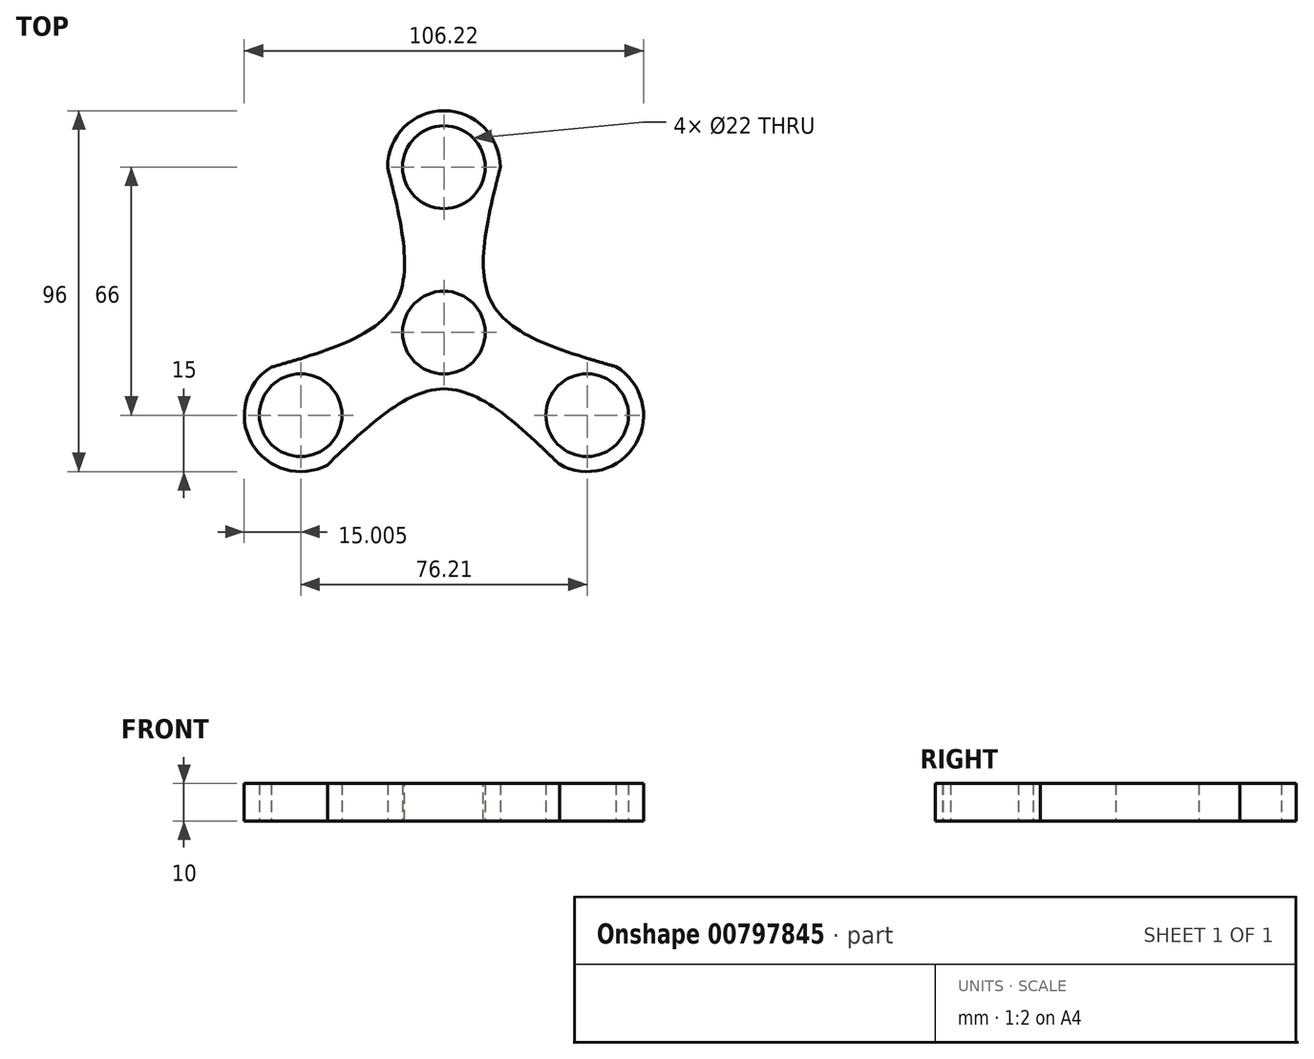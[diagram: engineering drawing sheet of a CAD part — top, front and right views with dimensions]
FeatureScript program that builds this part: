
annotation { "Feature Type Name" : "Feature", "Feature Type Description" : "" }
export const myFeature = defineFeature(function(context is Context, id is Id, definition is map)
    precondition{}
    {
        {
            var Q0;
            Q0=qCreatedBy(makeId("Top.planeOp"),FACE);
            var sketch = newSketch(context, id + "F0", { "sketchPlane" : qUnion([Q0])});
            skCircle(sketch, "E0", {"center": v(0, 0) * mm, "radius": 11 * mm});
            skCircle(sketch, "E1", {"center": v(0, 44) * mm, "radius": 11 * mm});
            skCircle(sketch, "E2", {"center": v(-38.1, -22) * mm, "radius": 11 * mm});
            skCircle(sketch, "E3", {"center": v(38.1, -22) * mm, "radius": 11 * mm});
            skCircle(sketch, "E4", {"center": v(-38.1, -22) * mm, "radius": 15 * mm});
            skCircle(sketch, "E5", {"center": v(0, 44) * mm, "radius": 15 * mm});
            skCircle(sketch, "E6", {"center": v(38.1, -22) * mm, "radius": 15 * mm});
            skCircle(sketch, "E7", {"center": v(0, 0) * mm, "radius": 15 * mm});
            skPoint(sketch, "E8", {"position": v(-45.97, -9.23) * mm});
            skPoint(sketch, "E9", {"position": v(-30.98, -35.2) * mm});
            skPoint(sketch, "E10", {"position": v(-15, 44) * mm});
            skPoint(sketch, "E11", {"position": v(15, 44) * mm});
            skPoint(sketch, "E12", {"position": v(45.72, -9.08) * mm});
            skPoint(sketch, "E13", {"position": v(-13, 7.5) * mm});
            skPoint(sketch, "E14", {"position": v(13, 7.5) * mm});
            skPoint(sketch, "E15", {"position": v(0, -15) * mm});
            skFitSpline(sketch, "E16", {"points": [v(-45.97, -9.23) * mm, v(-13, 7.5) * mm, v(-15, 44) * mm], "startDerivative": vector(84.47, 24.33) * mm, "endDerivative": vector(-21.2, 84.73) * mm});
            skFitSpline(sketch, "E17", {"points": [v(15, 44) * mm, v(13, 7.5) * mm, v(45.72, -9.08) * mm], "startDerivative": vector(-21.13, -84.64) * mm, "endDerivative": vector(84.02, -24.11) * mm});
            skPoint(sketch, "E18", {"position": v(30.72, -35.06) * mm});
            skFitSpline(sketch, "E19", {"points": [v(-30.98, -35.2) * mm, v(0, -15) * mm, v(30.72, -35.06) * mm], "startDerivative": vector(63.33, 61.04) * mm, "endDerivative": vector(62.97, -60.85) * mm});
            skSolve(sketch);
        }
        {
            var Q0;
            {var subQ0=sQuery(id+"F0.wireOp",EDGE,"E16");var subQ1=sQuery(id+"F0.wireOp",EDGE,"E4");var subQ2=makeQuery(id+"F0.imprint","INTERSECT",VERTEX,{"disambiguationData":[OD(1.0)],"derivedFrom":[subQ1,subQ0]});Q0=makeQuery(id+"F0.imprint","IMPRINT",FACE,{"disambiguationData":[TD([[makeQuery(id+"F0.imprint","IMPRINT",EDGE,{"disambiguationData":[TD([[subQ2,1.0]])],"derivedFrom":subQ1}),-1.0]])]});}
            var Q1;
            {var subQ0=sQuery(id+"F0.wireOp",EDGE,"E17");var subQ1=sQuery(id+"F0.wireOp",EDGE,"E6");var subQ2=makeQuery(id+"F0.imprint","INTERSECT",VERTEX,{"disambiguationData":[OD(1.0)],"derivedFrom":[subQ1,subQ0]});Q1=makeQuery(id+"F0.imprint","IMPRINT",FACE,{"disambiguationData":[TD([[makeQuery(id+"F0.imprint","IMPRINT",EDGE,{"disambiguationData":[TD([[subQ2,-1.0]])],"derivedFrom":subQ1}),-1.0]])]});}
            var Q2;
            {var subQ0=sQuery(id+"F0.wireOp",EDGE,"E16");var subQ1=sQuery(id+"F0.wireOp",EDGE,"E5");var subQ2=makeQuery(id+"F0.imprint","INTERSECT",VERTEX,{"disambiguationData":[OD(1.0)],"derivedFrom":[subQ1,subQ0]});Q2=makeQuery(id+"F0.imprint","IMPRINT",FACE,{"disambiguationData":[TD([[makeQuery(id+"F0.imprint","IMPRINT",EDGE,{"disambiguationData":[TD([[subQ2,-1.0]])],"derivedFrom":subQ1}),-1.0]])]});}
            var Q3;
            Q3=makeQuery(id+"F0.imprint","IMPRINT",FACE,{"disambiguationData":[TD([[makeQuery(id+"F0.imprint","IMPRINT",EDGE,{"derivedFrom":sQuery(id+"F0.wireOp",EDGE,"E2")}),-1.0]])]});
            var Q4;
            Q4=makeQuery(id+"F0.imprint","IMPRINT",FACE,{"disambiguationData":[TD([[makeQuery(id+"F0.imprint","IMPRINT",EDGE,{"derivedFrom":sQuery(id+"F0.wireOp",EDGE,"E3")}),-1.0]])]});
            var Q5;
            Q5=makeQuery(id+"F0.imprint","IMPRINT",FACE,{"disambiguationData":[TD([[makeQuery(id+"F0.imprint","IMPRINT",EDGE,{"derivedFrom":sQuery(id+"F0.wireOp",EDGE,"E0")}),-1.0]])]});
            var Q6;
            Q6=makeQuery(id+"F0.imprint","IMPRINT",FACE,{"disambiguationData":[TD([[makeQuery(id+"F0.imprint","IMPRINT",EDGE,{"derivedFrom":sQuery(id+"F0.wireOp",EDGE,"E1")}),-1.0]])]});
            extrude(context, id + "F1", {"entities" : qUnion([Q0, Q1, Q2, Q3, Q4, Q5, Q6]), "depth" : 10 * mm, "offsetDistance" : 25 * mm});
        }
    });
